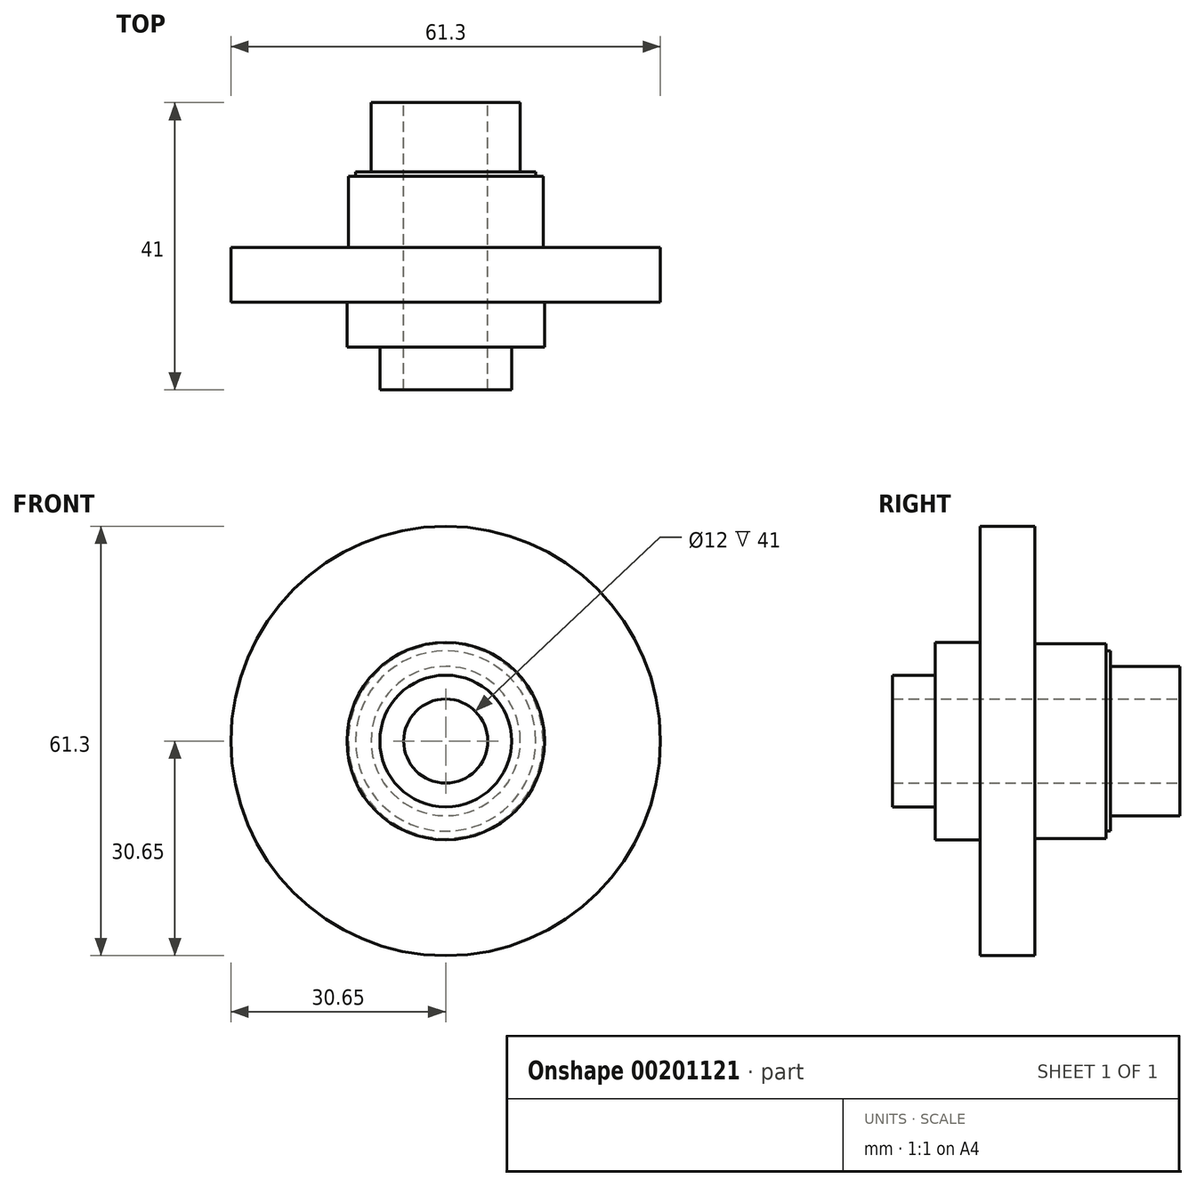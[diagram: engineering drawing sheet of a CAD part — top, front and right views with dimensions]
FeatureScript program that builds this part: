
annotation { "Feature Type Name" : "Feature", "Feature Type Description" : "" }
export const myFeature = defineFeature(function(context is Context, id is Id, definition is map)
    precondition{}
    {
        {
            var Q0;
            Q0=qCreatedBy(makeId("Front.planeOp"),FACE);
            var sketch = newSketch(context, id + "F0", { "sketchPlane" : qUnion([Q0])});
            skCircle(sketch, "E0", {"center": v(0, 0) * mm, "radius": 30.65 * mm});
            skCircle(sketch, "E1", {"center": v(0, 0) * mm, "radius": 6 * mm});
            skSolve(sketch);
        }
        {
            var Q0;
            Q0=makeQuery(id+"F0.imprint","IMPRINT",FACE,{"disambiguationData":[TD([[makeQuery(id+"F0.imprint","IMPRINT",EDGE,{"derivedFrom":sQuery(id+"F0.wireOp",EDGE,"E0")}),1.0]])]});
            extrude(context, id + "F1", {"entities" : qUnion([Q0]), "endBound" : BoundingType.SYMMETRIC, "depth" : 7.8 * mm, "offsetDistance" : 25 * mm});
        }
        {
            var Q0;
            Q0=makeQuery(id+"F1.opExtrude","CAP_FACE",FACE,{"disambiguationData":[OSD([sQuery(id+"F0.wireOp",EDGE,"E0")])],"isStart":false});
            var sketch = newSketch(context, id + "F2", { "sketchPlane" : qUnion([Q0])});
            skCircle(sketch, "E2", {"center": v(0, 0) * mm, "radius": 14.1 * mm});
            skSolve(sketch);
        }
        {
            var Q0;
            Q0=makeQuery(id+"F2.imprint","IMPRINT",FACE,{"disambiguationData":[TD([[makeQuery(id+"F2.imprint","IMPRINT",EDGE,{"derivedFrom":sQuery(id+"F2.wireOp",EDGE,"E2")}),1.0]])]});
            extrude(context, id + "F3", {"entities" : qUnion([Q0]), "operationType" : NewBodyOperationType.ADD, "depth" : 6.4 * mm, "offsetDistance" : 25 * mm});
        }
        {
            var Q0;
            Q0=makeQuery(id+"F3.opExtrude","CAP_FACE",FACE,{"disambiguationData":[OSD([sQuery(id+"F2.wireOp",EDGE,"E2")])],"isStart":false});
            var sketch = newSketch(context, id + "F4", { "sketchPlane" : qUnion([Q0])});
            skCircle(sketch, "E3", {"center": v(0, 0) * mm, "radius": 9.4 * mm});
            skSolve(sketch);
        }
        {
            var Q0;
            Q0=makeQuery(id+"F4.imprint","IMPRINT",FACE,{"disambiguationData":[TD([[makeQuery(id+"F4.imprint","IMPRINT",EDGE,{"derivedFrom":sQuery(id+"F4.wireOp",EDGE,"E3")}),1.0]])]});
            extrude(context, id + "F5", {"entities" : qUnion([Q0]), "operationType" : NewBodyOperationType.ADD, "depth" : 6.1 * mm, "offsetDistance" : 25 * mm});
        }
        {
            var Q0;
            Q0=makeQuery(id+"F1.opExtrude","CAP_FACE",FACE,{"disambiguationData":[OSD([sQuery(id+"F0.wireOp",EDGE,"E0")])],"isStart":true});
            var sketch = newSketch(context, id + "F6", { "sketchPlane" : qUnion([Q0])});
            skCircle(sketch, "E4", {"center": v(0, 0) * mm, "radius": 13.9 * mm});
            skSolve(sketch);
        }
        {
            var Q0;
            Q0 = qSketchRegion(id + "F6", true);
            extrude(context, id + "F7", {"entities" : qUnion([Q0]), "operationType" : NewBodyOperationType.ADD, "depth" : 10.2 * mm, "offsetDistance" : 25 * mm});
        }
        {
            var Q0;
            Q0=makeQuery(id+"F7.opExtrude","CAP_FACE",FACE,{"disambiguationData":[OSD([sQuery(id+"F6.wireOp",EDGE,"E4")])],"isStart":false});
            var sketch = newSketch(context, id + "F8", { "sketchPlane" : qUnion([Q0])});
            skCircle(sketch, "E5", {"center": v(0, 0) * mm, "radius": 12.88 * mm});
            skSolve(sketch);
        }
        {
            var Q0;
            Q0 = qSketchRegion(id + "F8", true);
            extrude(context, id + "F9", {"entities" : qUnion([Q0]), "operationType" : NewBodyOperationType.ADD, "depth" : 0.6 * mm, "offsetDistance" : 25 * mm});
        }
        {
            var Q0;
            Q0=makeQuery(id+"F9.opExtrude","CAP_FACE",FACE,{"disambiguationData":[OSD([sQuery(id+"F8.wireOp",EDGE,"E5")])],"isStart":false});
            var sketch = newSketch(context, id + "F10", { "sketchPlane" : qUnion([Q0])});
            skCircle(sketch, "E6", {"center": v(0, 0) * mm, "radius": 10.66 * mm});
            skSolve(sketch);
        }
        {
            var Q0;
            Q0 = qSketchRegion(id + "F10", true);
            extrude(context, id + "F11", {"entities" : qUnion([Q0]), "operationType" : NewBodyOperationType.ADD, "depth" : 9.9 * mm, "offsetDistance" : 25 * mm});
        }
        {
            var Q0;
            Q0=makeQuery(id+"F0.imprint","IMPRINT",FACE,{"disambiguationData":[TD([[makeQuery(id+"F0.imprint","IMPRINT",EDGE,{"derivedFrom":sQuery(id+"F0.wireOp",EDGE,"E1")}),1.0]])]});
            extrude(context, id + "F12", {"entities" : qUnion([Q0]), "operationType" : NewBodyOperationType.REMOVE, "endBound" : BoundingType.THROUGH_ALL, "oppositeDirection" : true, "depth" : 25 * mm, "offsetDistance" : 25 * mm});
        }
    });
